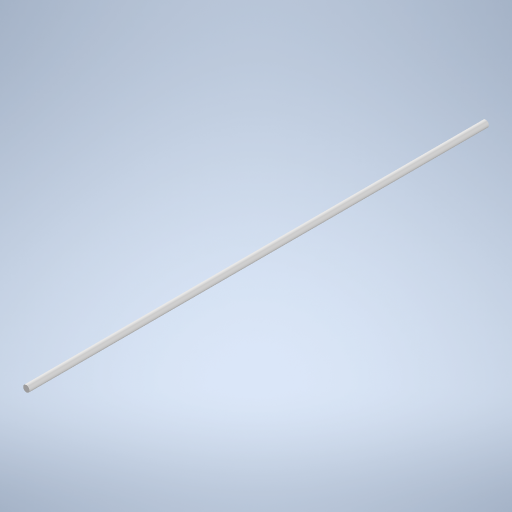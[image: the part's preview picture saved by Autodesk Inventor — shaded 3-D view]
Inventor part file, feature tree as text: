
AUTODESK INVENTOR PART (.ipt)
format: ipt  version: 2024.2 (Build 282272000, 272)  size: 239,616 bytes
history: native  units: mm
features: other x1, extrude x1, sketch x1
ambient origin geometry x8: Origin, YZ Plane, XZ Plane, XY Plane, X Axis, Y Axis, Z Axis, Center Point
bodies: Body1 (feature_tree)
feature tree (3):
  other  "Bryła1"
  extrude  "Wyciągnięcie proste1"  Depth=6.0mm
  sketch  "Szkic1"
